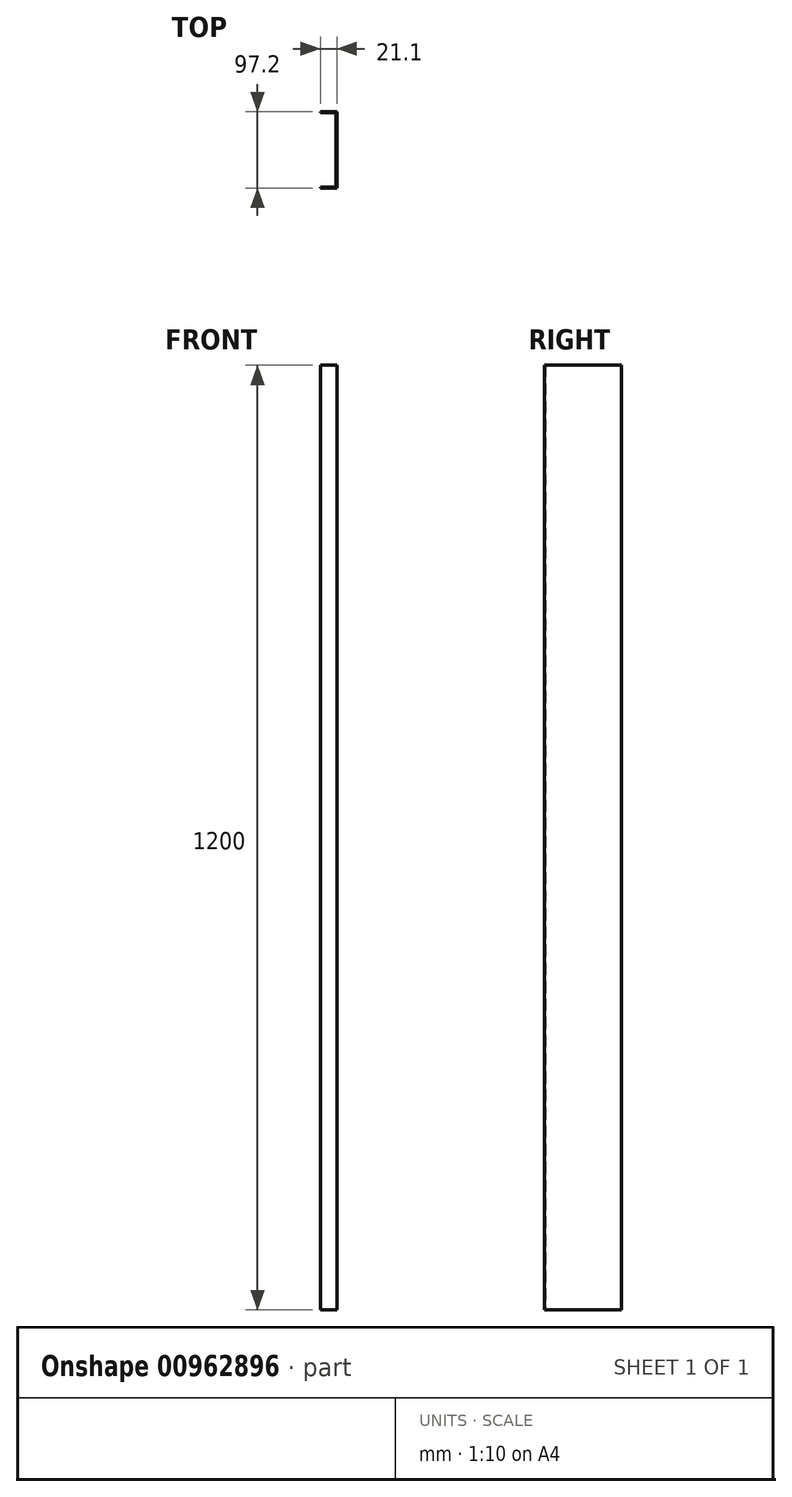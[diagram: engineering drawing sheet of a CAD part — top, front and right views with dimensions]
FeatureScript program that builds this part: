
annotation { "Feature Type Name" : "Feature", "Feature Type Description" : "" }
export const myFeature = defineFeature(function(context is Context, id is Id, definition is map)
    precondition{}
    {
        {
            var Q0;
            Q0=qCreatedBy(makeId("Top.planeOp"),FACE);
            var sketch = newSketch(context, id + "F0", { "sketchPlane" : qUnion([Q0])});
            skLineSegment(sketch, "E0.bottom", {"start": v(0, 0) * mm, "end": v(20, 0) * mm});
            skLineSegment(sketch, "E0.top", {"start": v(0, -95) * mm, "end": v(20, -95) * mm});
            skLineSegment(sketch, "E0.right", {"start": v(20, 0) * mm, "end": v(20, -95) * mm});
            skLineSegment(sketch, "E1.0", {"start": v(0, -96.1) * mm, "end": v(21.1, -96.1) * mm});
            skLineSegment(sketch, "E1.1", {"start": v(21.1, 1.1) * mm, "end": v(21.1, -96.1) * mm});
            skLineSegment(sketch, "E1.2", {"start": v(0, 1.1) * mm, "end": v(21.1, 1.1) * mm});
            skLineSegment(sketch, "E2", {"start": v(0, 1.1) * mm, "end": v(0, 0) * mm});
            skLineSegment(sketch, "E3", {"start": v(0, -95) * mm, "end": v(0, -96.1) * mm});
            skSolve(sketch);
        }
        {
            var Q0;
            Q0 = qSketchRegion(id + "F0", true);
            extrude(context, id + "F1", {"entities" : qUnion([Q0]), "depth" : 1200 * mm, "offsetDistance" : 25 * mm});
        }
    });
